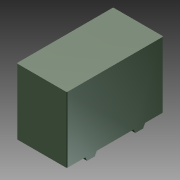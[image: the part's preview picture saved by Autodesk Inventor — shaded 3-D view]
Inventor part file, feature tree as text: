
AUTODESK INVENTOR PART (.ipt)
format: ipt  version: 2011 SP1 (Build 150282100, 282)  size: 110,080 bytes
history: native  units: in
note: dims shown in document units (in); Inventor stores cm internally (conversion verified against a paired STEP export)
features: other x21, extrude x5, sketch x5
ambient origin geometry x8: Origin, YZ Plane, XZ Plane, XY Plane, X Axis, Y Axis, Z Axis, Center Point
bodies: Solid1 (feature_tree)
feature tree (31):
  extrude  "Extrusion1"  Depth=0.025in TaperAngle=0.0deg
  extrude  "Extrusion2"  Depth=0.025in TaperAngle=0.0deg
  extrude  "Extrusion3"  [1 undecoded]
  extrude  "Extrusion4"  [1 undecoded]
  extrude  "Extrusion5"  [1 undecoded]
  other  "bushing_XY"
  other  "bushing_YZ"
  other  "bushing_ZX"
  other  "bushing_X"
  other  "bushing_Y"
  other  "bushing_Z"
  other  "bushing_Center"
  other  "dummy_body_XY"
  other  "dummy_body_YZ"
  other  "dummy_body_ZX"
  other  "dummy_body_X"
  other  "dummy_body_Y"
  other  "dummy_body_Z"
  other  "dummy_body_Center"
  other  "terminals_XY"
  other  "terminals_YZ"
  other  "terminals_ZX"
  other  "terminals_X"
  other  "terminals_Y"
  other  "terminals_Z"
  other  "terminals_Center"
  sketch  "Sketch_1"  dims[d0=0.34in d1=0.0in d2=0.025in d3=0.0in]
  sketch  "Sketch_2"  dims[d4=0.025in d5=0.0in d6=0.025in d7=0.0in]
  sketch  "Sketch_3"  dims[d8=0.025in d9=0.0in]
  sketch  "Sketch_4"
  sketch  "Sketch_5"
note: 3 required parameter values undecoded (feature->parameter linkage not recoverable at this tier; creation-order binding heuristic only, values carry confidence <= 0.55)
